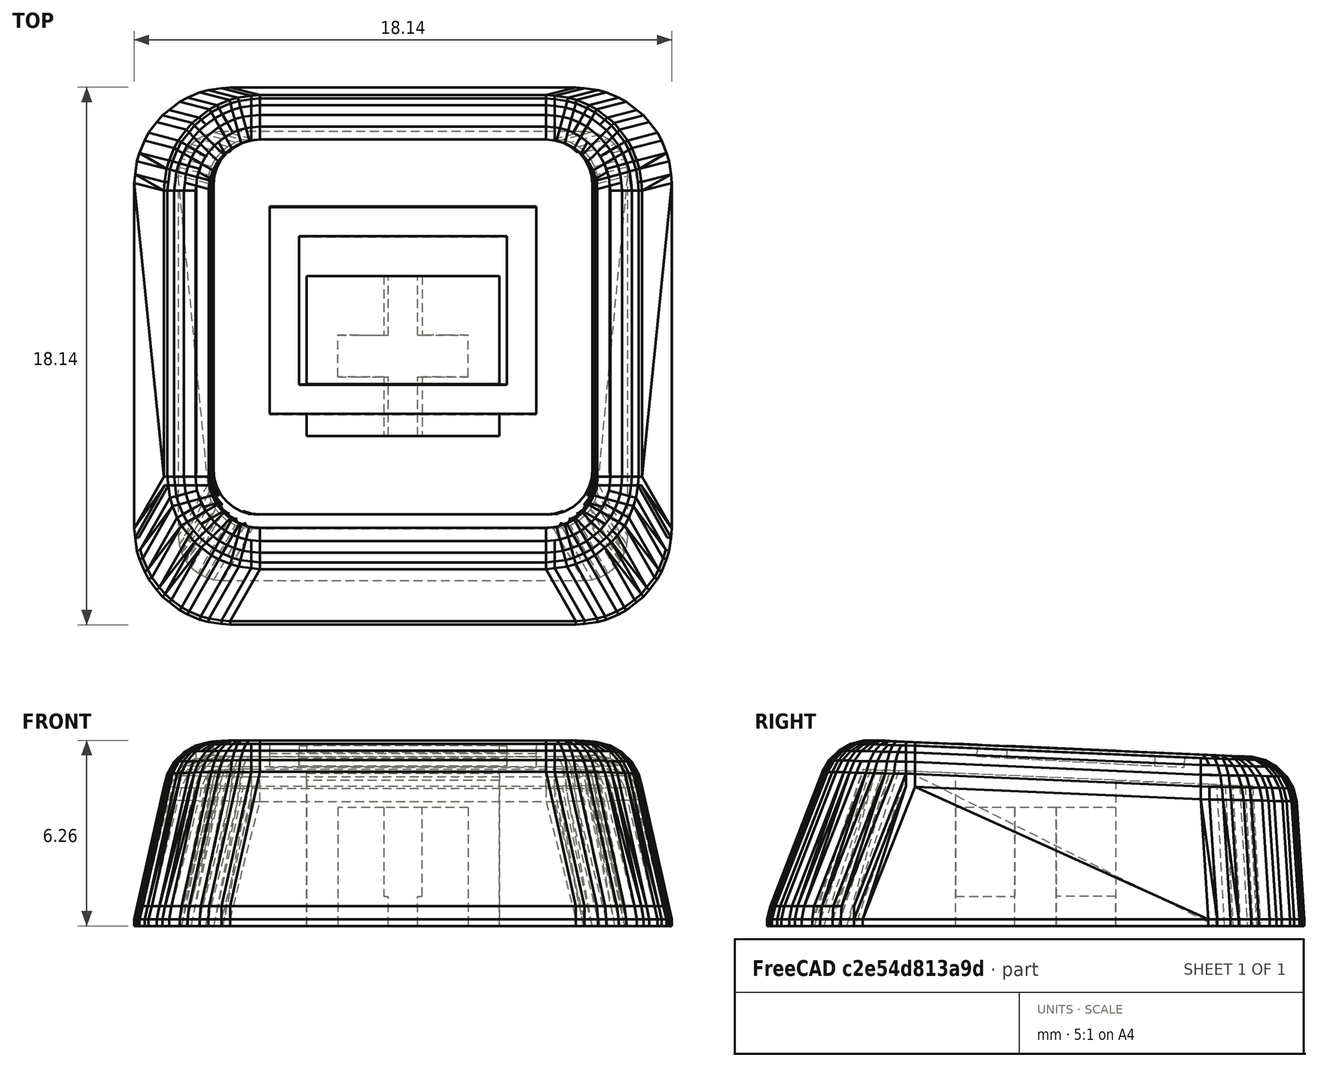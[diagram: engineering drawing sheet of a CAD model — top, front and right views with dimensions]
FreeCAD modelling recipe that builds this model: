
FCSTD DOCUMENT  (FreeCAD 0.18R16131 (Git))
Label: screen_off
License: All rights reserved
LicenseURL: http://en.wikipedia.org/wiki/All_rights_reserved
objects: Part::Box×6, Part::Cut×2, Part::Feature×1, Part::MultiFuse×1
note: 10 computed .brp shape members not serialized (recipe doc carries the construction recipe); baked Part::Feature solids carry a one-line shape summary decoded from their .brp

FEATURE [Part::Feature] Solid
  shape: bbox 18.13 x 18.13 x 6.262 mm, 1259 faces (baked)
FEATURE [Part::Box] Box  label="Cube"
  AttacherType = Attacher::AttachEngine3D
  Height = 1
  Length = 1
  Placement = pos=(0.5,-2.7,0) rot=(0,0,1;0rad)
  Width = 2
FEATURE [Part::Box] Box001  label="Cube001"
  AttacherType = Attacher::AttachEngine3D
  Height = 1
  Length = 1
  Placement = pos=(-1.5,0.7,0) rot=(0,0,1;0rad)
  Width = 2
FEATURE [Part::Box] Box002  label="Cube002"
  AttacherType = Attacher::AttachEngine3D
  Height = 1
  Length = 1
  Placement = pos=(-1.5,-2.7,0) rot=(0,0,1;0rad)
  Width = 2
FEATURE [Part::Box] Box003  label="Cube003"
  AttacherType = Attacher::AttachEngine3D
  Height = 1
  Length = 1
  Placement = pos=(0.5,0.7,0) rot=(0,0,1;0rad)
  Width = 2
FEATURE [Part::MultiFuse] Fusion
  Shapes = -> [Solid,Box002,Box001,Box,Box003]
FEATURE [Part::Box] Box004  label="Cube004"
  AttacherType = Attacher::AttachEngine3D
  Height = 0.5
  Length = 9
  Placement = pos=(-4.5,-2.5,10) rot=(0,0,1;0rad)
  Width = 7
FEATURE [Part::Box] Box005  label="Cube005"
  AttacherType = Attacher::AttachEngine3D
  Height = 0.5
  Length = 7
  Placement = pos=(-3.5,-1.5,10) rot=(0,0,1;0rad)
  Width = 5
FEATURE [Part::Cut] Cut
  Base = -> Box004
  Placement = pos=(0,0,-4.4) rot=(1,0,0;-0.05236rad)
  Tool = -> Box005
FEATURE [Part::Cut] Cut001
  Base = -> Fusion
  Tool = -> Cut
